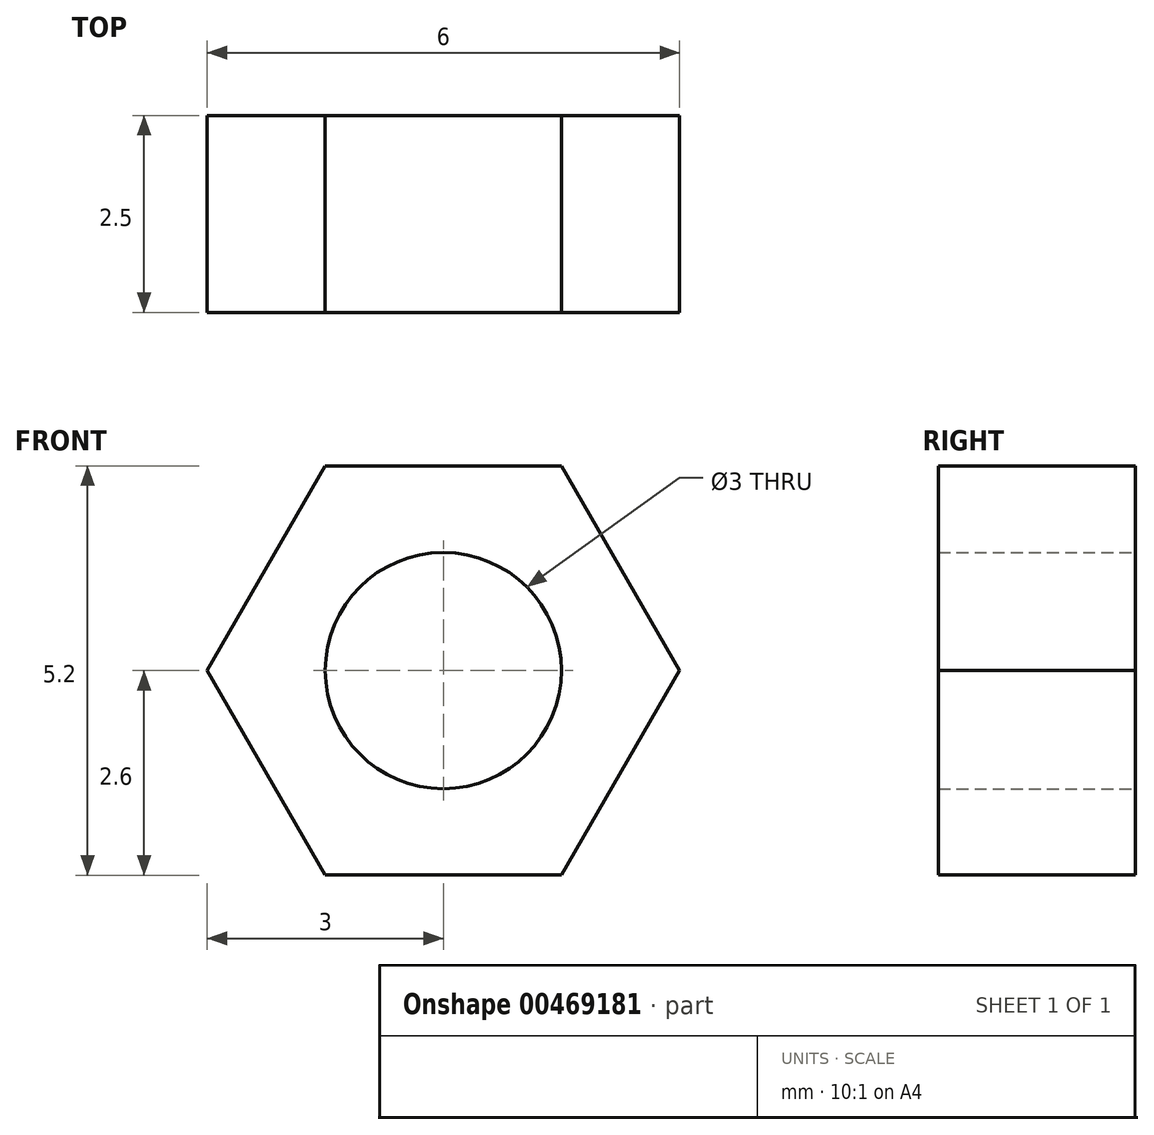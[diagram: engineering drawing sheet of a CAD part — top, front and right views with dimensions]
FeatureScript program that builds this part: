
annotation { "Feature Type Name" : "Feature", "Feature Type Description" : "" }
export const myFeature = defineFeature(function(context is Context, id is Id, definition is map)
    precondition{}
    {
        {
            var Q0;
            Q0=qCreatedBy(makeId("Front.planeOp"),FACE);
            var sketch = newSketch(context, id + "F0", { "sketchPlane" : qUnion([Q0])});
            skCircle(sketch, "E0.cCircle", {"center": v(0, 0) * mm, "radius": 3 * mm, "construction": true});
            skLineSegment(sketch, "E0.0", {"start": v(3, 0) * mm, "end": v(1.5, -2.6) * mm});
            skLineSegment(sketch, "E0.1", {"start": v(1.5, -2.6) * mm, "end": v(-1.5, -2.6) * mm});
            skLineSegment(sketch, "E0.2", {"start": v(-1.5, -2.6) * mm, "end": v(-3, 0) * mm});
            skLineSegment(sketch, "E0.3", {"start": v(-3, 0) * mm, "end": v(-1.5, 2.6) * mm});
            skLineSegment(sketch, "E0.4", {"start": v(-1.5, 2.6) * mm, "end": v(1.5, 2.6) * mm});
            skLineSegment(sketch, "E0.5", {"start": v(1.5, 2.6) * mm, "end": v(3, 0) * mm});
            skCircle(sketch, "E1", {"center": v(0, 0) * mm, "radius": 1.5 * mm});
            skSolve(sketch);
        }
        {
            var Q0;
            Q0=makeQuery(id+"F0.imprint","IMPRINT",FACE,{"disambiguationData":[TD([[makeQuery(id+"F0.imprint","IMPRINT",EDGE,{"derivedFrom":sQuery(id+"F0.wireOp",EDGE,"E0.0")}),-1.0]])]});
            extrude(context, id + "F1", {"entities" : qUnion([Q0]), "depth" : 2.5 * mm});
        }
    });
